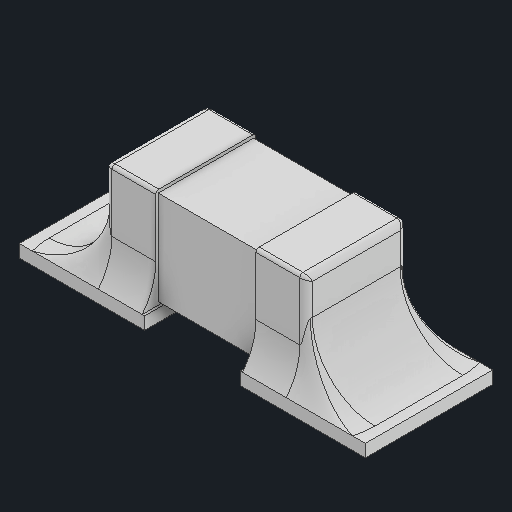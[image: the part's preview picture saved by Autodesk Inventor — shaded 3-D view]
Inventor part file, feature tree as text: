
AUTODESK INVENTOR PART (.ipt)
format: ipt  version: 2023 (Build 270158000, 158)  size: 195,072 bytes
history: native  units: in
note: dims shown in document units (in); Inventor stores cm internally (conversion verified against a paired STEP export)
features: fillet x1
ambient origin geometry x8: Origin, YZ Plane, XZ Plane, XY Plane, X Axis, Y Axis, Z Axis, Center Point
bodies: Solid1 (feature_tree)
feature tree (1):
  fillet  "Fillet5"  [1 undecoded]
note: 1 required parameter value undecoded (feature->parameter linkage not recoverable at this tier; creation-order binding heuristic only, values carry confidence <= 0.55)
